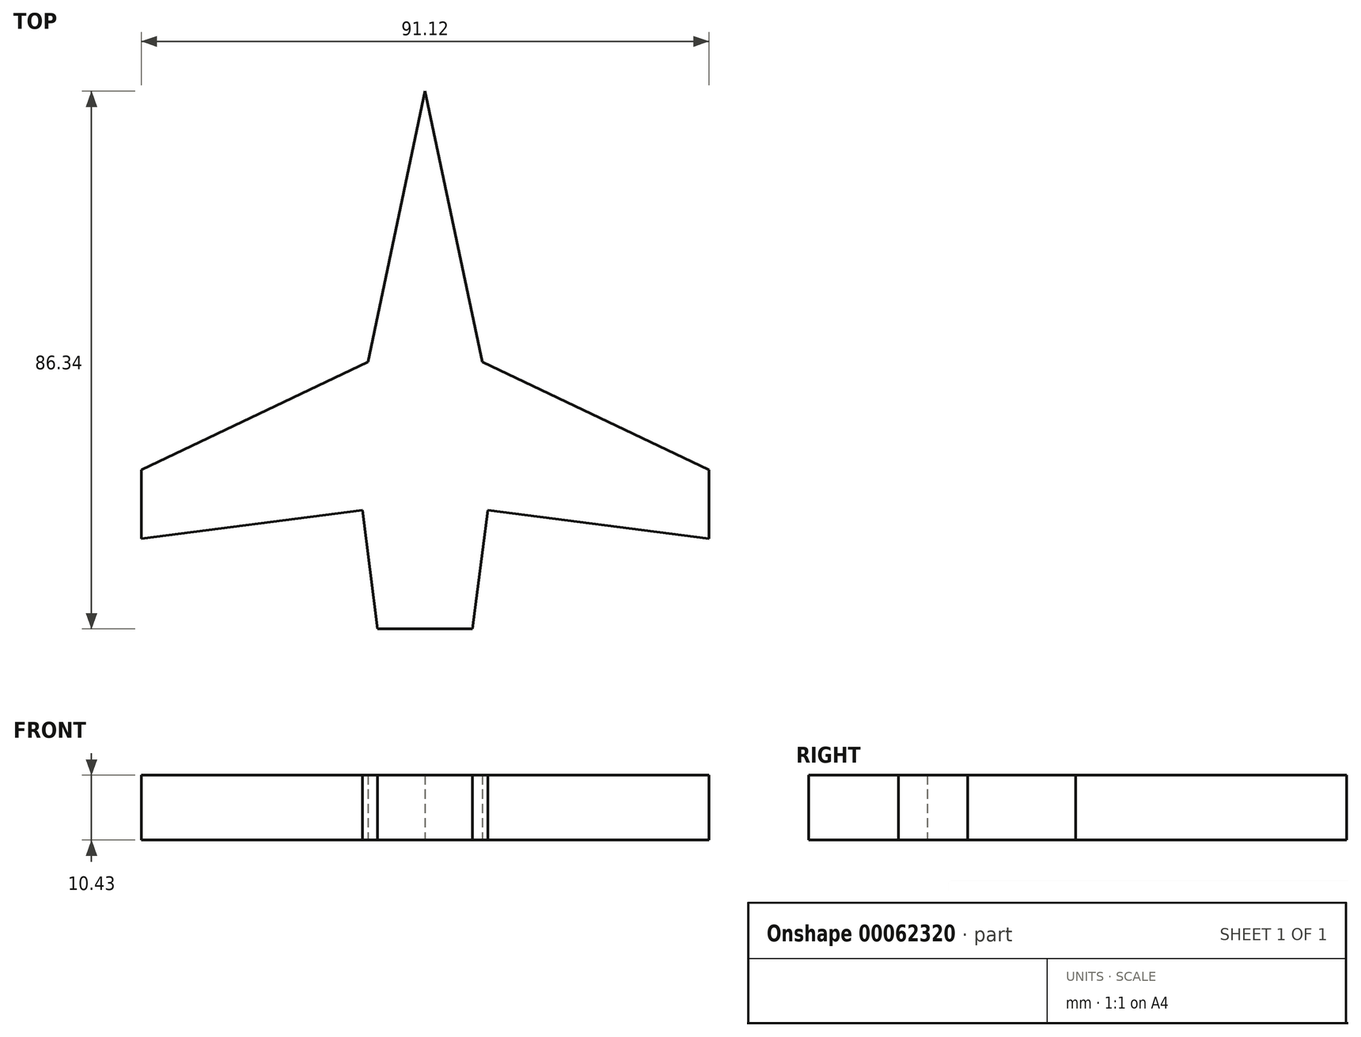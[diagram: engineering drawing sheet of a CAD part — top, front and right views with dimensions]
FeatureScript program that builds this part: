
annotation { "Feature Type Name" : "Feature", "Feature Type Description" : "" }
export const myFeature = defineFeature(function(context is Context, id is Id, definition is map)
    precondition{}
    {
        {
            var Q0;
            Q0=qCreatedBy(makeId("Top.planeOp"),FACE);
            var sketch = newSketch(context, id + "F0", { "sketchPlane" : qUnion([Q0])});
            skLineSegment(sketch, "E0", {"start": v(0, 60.78) * mm, "end": v(9.16, 17.28) * mm});
            skLineSegment(sketch, "E1", {"start": v(9.16, 17.28) * mm, "end": v(45.56, 0) * mm});
            skLineSegment(sketch, "E2", {"start": v(45.56, 0) * mm, "end": v(45.56, -11.1) * mm});
            skLineSegment(sketch, "E3", {"start": v(45.56, -11.1) * mm, "end": v(10.07, -6.52) * mm});
            skLineSegment(sketch, "E4", {"start": v(10.07, -6.52) * mm, "end": v(7.62, -25.56) * mm});
            skLineSegment(sketch, "E5", {"start": v(7.62, -25.56) * mm, "end": v(0, -25.56) * mm});
            skLineSegment(sketch, "E6.MirrorCS", {"start": v(-7.62, -25.56) * mm, "end": v(0, -25.56) * mm});
            skLineSegment(sketch, "E7.MirrorCS", {"start": v(0, 60.78) * mm, "end": v(-9.16, 17.28) * mm});
            skLineSegment(sketch, "E8.MirrorCS", {"start": v(-10.07, -6.52) * mm, "end": v(-7.62, -25.56) * mm});
            skLineSegment(sketch, "E9.MirrorCS", {"start": v(-45.56, 0) * mm, "end": v(-45.56, -11.1) * mm});
            skLineSegment(sketch, "E10.MirrorCS", {"start": v(-45.56, -11.1) * mm, "end": v(-10.07, -6.52) * mm});
            skLineSegment(sketch, "E11.MirrorCS", {"start": v(-9.16, 17.28) * mm, "end": v(-45.56, 0) * mm});
            skSolve(sketch);
        }
        {
            var Q0;
            Q0=makeQuery(id+"F0.imprint","IMPRINT",FACE,{"disambiguationData":[TD([[makeQuery(id+"F0.imprint","IMPRINT",EDGE,{"derivedFrom":sQuery(id+"F0.wireOp",EDGE,"E0")}),-1.0]])]});
            extrude(context, id + "F1", {"entities" : qUnion([Q0]), "depth" : 10.43 * mm});
        }
    });
